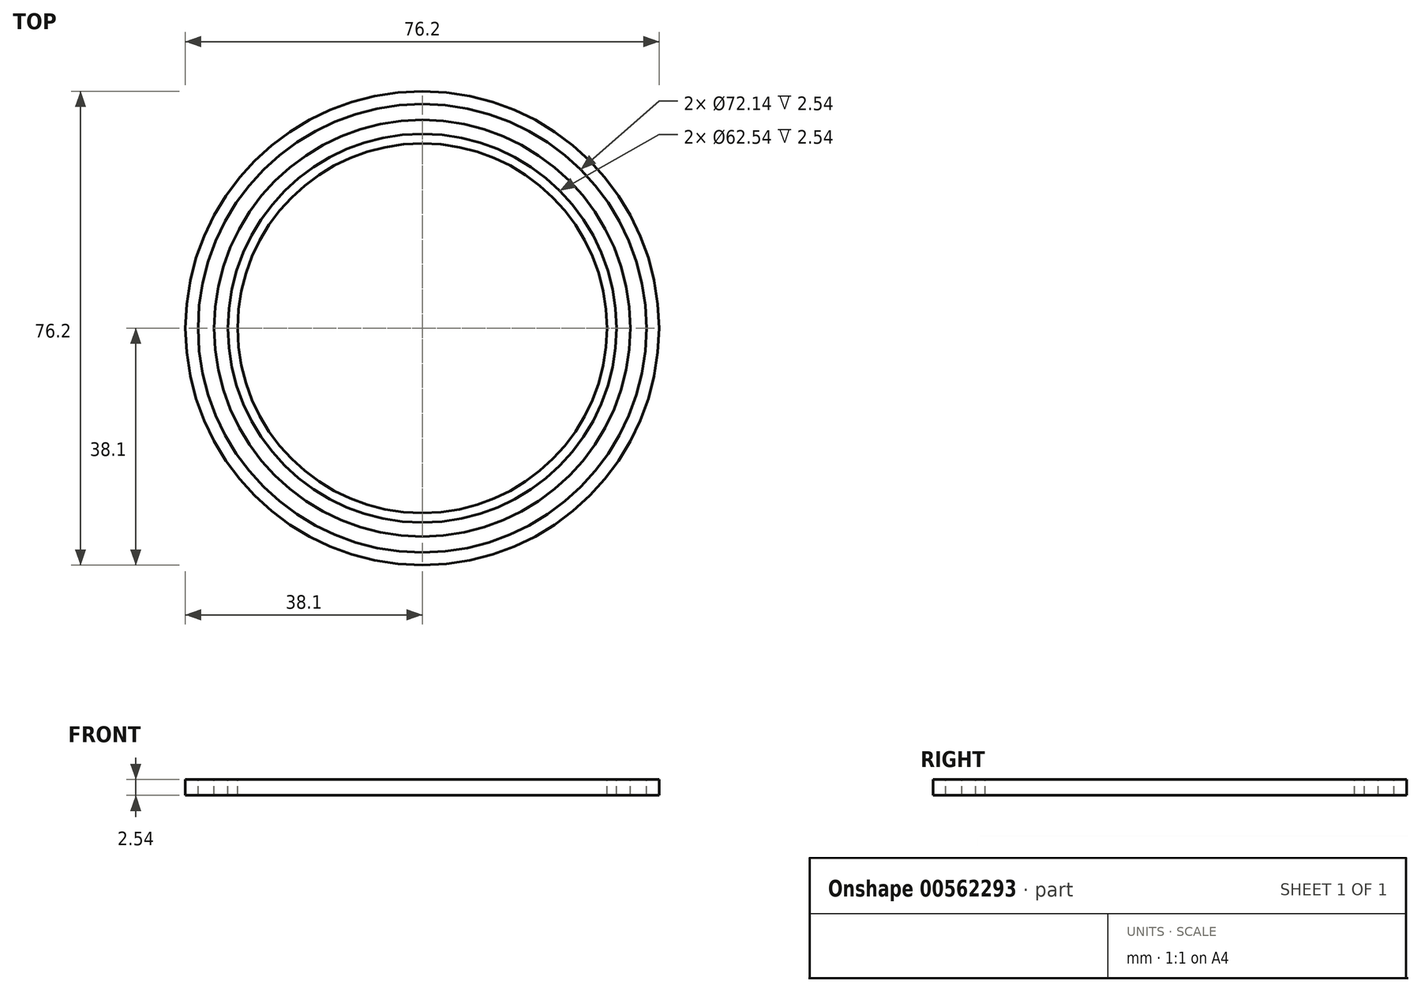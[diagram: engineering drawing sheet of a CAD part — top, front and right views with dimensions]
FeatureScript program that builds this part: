
annotation { "Feature Type Name" : "Feature", "Feature Type Description" : "" }
export const myFeature = defineFeature(function(context is Context, id is Id, definition is map)
    precondition{}
    {
        {
            var Q0;
            Q0=qCreatedBy(makeId("Top.planeOp"),FACE);
            var sketch = newSketch(context, id + "F0", { "sketchPlane" : qUnion([Q0])});
            skCircle(sketch, "E0", {"center": v(0, 0) * mm, "radius": 38.1 * mm});
            skSolve(sketch);
        }
        {
            var Q0;
            Q0 = qSketchRegion(id + "F0", true);
            extrude(context, id + "F1", {"entities" : qUnion([Q0]), "depth" : 2.54 * mm, "offsetDistance" : 25.4 * mm});
        }
        {
            var Q0;
            Q0=makeQuery(id+"F1.opExtrude","CAP_FACE",FACE,{"disambiguationData":[OSD([sQuery(id+"F0.wireOp",EDGE,"E0")])],"isStart":false});
            var sketch = newSketch(context, id + "F2", { "sketchPlane" : qUnion([Q0])});
            skCircle(sketch, "E1", {"center": v(0, 0) * mm, "radius": 36.07 * mm});
            skCircle(sketch, "E2", {"center": v(0, 0) * mm, "radius": 33.5 * mm});
            skCircle(sketch, "E3", {"center": v(0, 0) * mm, "radius": 31.8 * mm});
            skSolve(sketch);
        }
        {
            var Q0;
            Q0=makeQuery(id+"F2.imprint","IMPRINT",FACE,{"disambiguationData":[TD([[makeQuery(id+"F2.imprint","IMPRINT",EDGE,{"derivedFrom":sQuery(id+"F2.wireOp",EDGE,"E1")}),1.0]])]});
            var Q1;
            Q1=sQuery(id+"F2.wireOp",EDGE,"E2");
            extrude(context, id + "F3", {"entities" : qUnion([Q0]), "operationType" : NewBodyOperationType.REMOVE, "surfaceEntities" : qUnion([Q1]), "oppositeDirection" : true, "depth" : 25.4 * mm, "offsetDistance" : 25.4 * mm});
        }
        {
            var Q0;
            Q0=makeQuery(id+"F3.boolean.opBoolean","SPLIT",FACE,{"disambiguationData":[TD([makeQuery(id+"F3.opExtrude","SWEPT_FACE",FACE,{"disambiguationData":[OSD([sQuery(id+"F2.wireOp",EDGE,"E2")])]})])],"derivedFrom":makeQuery(id+"F1.opExtrude","CAP_FACE",FACE,{"disambiguationData":[OSD([sQuery(id+"F0.wireOp",EDGE,"E0")])],"isStart":false})});
            var sketch = newSketch(context, id + "F4", { "sketchPlane" : qUnion([Q0])});
            skCircle(sketch, "E4", {"center": v(0, 0) * mm, "radius": 31.27 * mm});
            skCircle(sketch, "E5", {"center": v(0, 0) * mm, "radius": 29.72 * mm});
            skSolve(sketch);
        }
        {
            var Q0;
            Q0=makeQuery(id+"F4.imprint","IMPRINT",FACE,{"disambiguationData":[TD([[makeQuery(id+"F4.imprint","IMPRINT",EDGE,{"derivedFrom":sQuery(id+"F4.wireOp",EDGE,"E4")}),1.0]])]});
            extrude(context, id + "F5", {"entities" : qUnion([Q0]), "operationType" : NewBodyOperationType.REMOVE, "oppositeDirection" : true, "depth" : 25.4 * mm, "offsetDistance" : 25.4 * mm});
        }
    });
